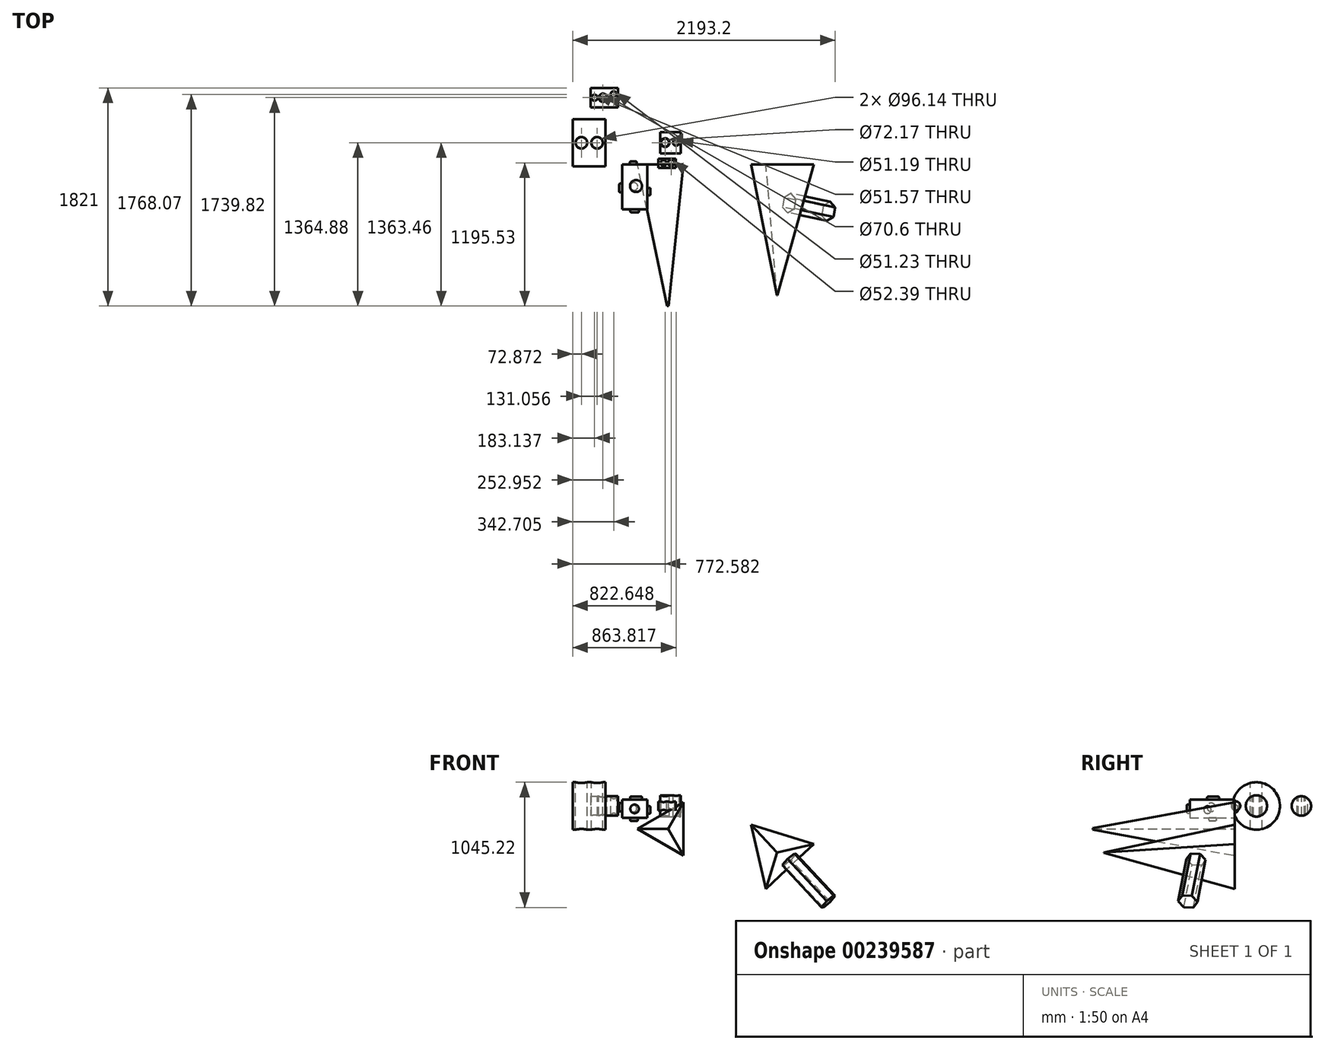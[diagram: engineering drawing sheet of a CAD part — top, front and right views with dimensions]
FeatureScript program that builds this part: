
annotation { "Feature Type Name" : "Feature", "Feature Type Description" : "" }
export const myFeature = defineFeature(function(context is Context, id is Id, definition is map)
    precondition{}
    {
        {
            var Q0;
            Q0=qCreatedBy(makeId("Front.planeOp"),FACE);
            var sketch = newSketch(context, id + "F0", { "sketchPlane" : qUnion([Q0])});
            skLineSegment(sketch, "E0", {"start": v(-145.02, 0) * mm, "end": v(178.73, 0) * mm});
            skLineSegment(sketch, "E1", {"start": v(-204, 52.6) * mm, "end": v(227.6, 52.6) * mm});
            skLineSegment(sketch, "E2", {"start": v(228.05, -98.9) * mm, "end": v(-210.3, -98.9) * mm});
            skLineSegment(sketch, "E3", {"start": v(81.85, 196.23) * mm, "end": v(81.85, -166.27) * mm});
            skLineSegment(sketch, "E4", {"start": v(-128.62, 137.85) * mm, "end": v(-128.62, -208.02) * mm});
            skSolve(sketch);
        }
        {
            var Q0;
            Q0 = qSketchRegion(id + "F0", true);
            extrude(context, id + "F1", {"entities" : qUnion([Q0]), "depth" : 373.9 * mm});
        }
        {
            var Q0;
            Q0=makeQuery(id+"F1.opExtrude","CAP_FACE",FACE,{"disambiguationData":[OSD([sQuery(id+"F0.wireOp",EDGE,"E1"),sQuery(id+"F0.wireOp",EDGE,"E2"),sQuery(id+"F0.wireOp",EDGE,"E3"),sQuery(id+"F0.wireOp",EDGE,"E4")])],"isStart":false});
            var sketch = newSketch(context, id + "F2", { "sketchPlane" : qUnion([Q0])});
            skCircle(sketch, "E5", {"center": v(-25.3, -24.2) * mm, "radius": 35.87 * mm});
            skSolve(sketch);
        }
        {
            var Q0;
            Q0 = qSketchRegion(id + "F2", true);
            extrude(context, id + "F3", {"entities" : qUnion([Q0]), "operationType" : NewBodyOperationType.ADD, "depth" : 25.4 * mm});
        }
        {
            var Q0;
            Q0=makeQuery(id+"F1.opExtrude","SWEPT_FACE",FACE,{"disambiguationData":[OSD([sQuery(id+"F0.wireOp",EDGE,"E3")])]});
            var sketch = newSketch(context, id + "F4", { "sketchPlane" : qUnion([Q0])});
            skCircle(sketch, "E6", {"center": v(-226.15, -32.57) * mm, "radius": 30.45 * mm});
            skSolve(sketch);
        }
        {
            var Q0;
            Q0 = qSketchRegion(id + "F4", true);
            extrude(context, id + "F5", {"entities" : qUnion([Q0]), "operationType" : NewBodyOperationType.ADD, "depth" : 25.4 * mm});
        }
        {
            var Q0;
            Q0=makeQuery(id+"F1.opExtrude","CAP_FACE",FACE,{"disambiguationData":[OSD([sQuery(id+"F0.wireOp",EDGE,"E1"),sQuery(id+"F0.wireOp",EDGE,"E2"),sQuery(id+"F0.wireOp",EDGE,"E3"),sQuery(id+"F0.wireOp",EDGE,"E4")])],"isStart":true});
            var sketch = newSketch(context, id + "F27", { "sketchPlane" : qUnion([Q0])});
            skCircle(sketch, "E7", {"center": v(36.05, -21.8) * mm, "radius": 28.54 * mm});
            skSolve(sketch);
        }
        {
            var Q0;
            Q0 = qSketchRegion(id + "F27", true);
            extrude(context, id + "F6", {"entities" : qUnion([Q0]), "operationType" : NewBodyOperationType.ADD, "depth" : 25.4 * mm});
        }
        {
            var Q0;
            Q0=makeQuery(id+"F1.opExtrude","SWEPT_FACE",FACE,{"disambiguationData":[OSD([sQuery(id+"F0.wireOp",EDGE,"E4")])]});
            var sketch = newSketch(context, id + "F7", { "sketchPlane" : qUnion([Q0])});
            skCircle(sketch, "E8", {"center": v(195.22, -10.7) * mm, "radius": 35.87 * mm});
            skSolve(sketch);
        }
        {
            var Q0;
            Q0 = qSketchRegion(id + "F7", true);
            extrude(context, id + "F8", {"entities" : qUnion([Q0]), "operationType" : NewBodyOperationType.ADD, "depth" : 25.4 * mm});
        }
        {
            var Q0;
            Q0=makeQuery(id+"F1.opExtrude","SWEPT_FACE",FACE,{"disambiguationData":[OSD([sQuery(id+"F0.wireOp",EDGE,"E1")])]});
            var sketch = newSketch(context, id + "F28", { "sketchPlane" : qUnion([Q0])});
            skCircle(sketch, "E9", {"center": v(-13.2, -179.26) * mm, "radius": 50 * mm});
            skSolve(sketch);
        }
        {
            var Q0;
            Q0 = qSketchRegion(id + "F28", true);
            extrude(context, id + "F9", {"entities" : qUnion([Q0]), "operationType" : NewBodyOperationType.ADD, "depth" : 25.4 * mm});
        }
        {
            var Q0;
            Q0=makeQuery(id+"F1.opExtrude","SWEPT_FACE",FACE,{"disambiguationData":[OSD([sQuery(id+"F0.wireOp",EDGE,"E2")])]});
            var sketch = newSketch(context, id + "F10", { "sketchPlane" : qUnion([Q0])});
            skCircle(sketch, "E10", {"center": v(-29.94, 183.6) * mm, "radius": 31.67 * mm});
            skSolve(sketch);
        }
        {
            var Q0;
            Q0 = qSketchRegion(id + "F10", true);
            extrude(context, id + "F11", {"entities" : qUnion([Q0]), "operationType" : NewBodyOperationType.ADD, "depth" : 25.4 * mm});
        }
        {
            var Q0;
            Q0=makeQuery(id+"F11.opExtrude","CAP_EDGE",EDGE,{"disambiguationData":[OSD([sQuery(id+"F10.wireOp",EDGE,"E10")])],"isStart":false});
            var Q1;
            Q1=makeQuery(id+"F8.opExtrude","CAP_EDGE",EDGE,{"disambiguationData":[OSD([sQuery(id+"F7.wireOp",EDGE,"E8")])],"isStart":false});
            var Q2;
            Q2=makeQuery(id+"F3.opExtrude","CAP_EDGE",EDGE,{"disambiguationData":[OSD([sQuery(id+"F2.wireOp",EDGE,"E5")])],"isStart":false});
            var Q3;
            Q3=makeQuery(id+"F6.opExtrude","CAP_EDGE",EDGE,{"disambiguationData":[OSD([sQuery(id+"F27.wireOp",EDGE,"E7")])],"isStart":false});
            var Q4;
            Q4=makeQuery(id+"F9.opExtrude","CAP_EDGE",EDGE,{"disambiguationData":[OSD([sQuery(id+"F28.wireOp",EDGE,"E9")])],"isStart":false});
            var Q5;
            Q5=makeQuery(id+"F5.opExtrude","CAP_EDGE",EDGE,{"disambiguationData":[OSD([sQuery(id+"F4.wireOp",EDGE,"E6")])],"isStart":false});
            fillet(context, id + "F12", {"entities" : qUnion([Q0, Q1, Q2, Q3, Q4, Q5]), "radius" : 7.95 * mm, "tangentPropagation" : true, "allowEdgeOverflow" : false});
        }
        {
            var Q0;
            Q0=qCreatedBy(makeId("Front.planeOp"),FACE);
            var sketch = newSketch(context, id + "F29", { "sketchPlane" : qUnion([Q0])});
            skCircle(sketch, "E11.cCircle", {"center": v(254.78, -191.8) * mm, "radius": 128.13 * mm, "construction": true});
            skLineSegment(sketch, "E11.0", {"start": v(382.92, 30.13) * mm, "end": v(382.92, -413.74) * mm});
            skLineSegment(sketch, "E11.1", {"start": v(382.92, -413.74) * mm, "end": v(-1.48, -191.8) * mm});
            skLineSegment(sketch, "E11.2", {"start": v(-1.48, -191.8) * mm, "end": v(382.92, 30.13) * mm});
            skPoint(sketch, "E11.0.midPoint", {"position": v(382.92, -191.8) * mm});
            skSolve(sketch);
        }
        {
            var Q0;
            Q0 = qSketchRegion(id + "F29", true);
            extrude(context, id + "F30", {"entities" : qUnion([Q0]), "depth" : 1182.1 * mm, "hasDraft" : true, "draftAngle" : 6 * degree, "draftPullDirection" : true});
        }
        {
            var Q0;
            Q0=qCreatedBy(makeId("Front.planeOp"),FACE);
            var sketch = newSketch(context, id + "F31", { "sketchPlane" : qUnion([Q0])});
            skCircle(sketch, "E12.cCircle", {"center": v(1163.63, -389.04) * mm, "radius": 316.45 * mm, "construction": true});
            skLineSegment(sketch, "E12.0", {"start": v(947.84, -157.57) * mm, "end": v(1471.98, -317.9) * mm});
            skLineSegment(sketch, "E12.1", {"start": v(1471.98, -317.9) * mm, "end": v(1071.05, -691.65) * mm});
            skLineSegment(sketch, "E12.2", {"start": v(1071.05, -691.65) * mm, "end": v(947.84, -157.57) * mm});
            skSolve(sketch);
        }
        {
            var Q0;
            Q0 = qSketchRegion(id + "F31", true);
            extrude(context, id + "F13", {"entities" : qUnion([Q0]), "depth" : 1090.3 * mm, "hasDraft" : true, "draftAngle" : 8.2 * degree, "draftPullDirection" : true});
        }
        {
            var Q0;
            Q0=makeQuery(id+"F13.opExtrude","SWEPT_FACE",FACE,{"disambiguationData":[OSD([sQuery(id+"F31.wireOp",EDGE,"E12.1")])]});
            var sketch = newSketch(context, id + "F32", { "sketchPlane" : qUnion([Q0])});
            skCircle(sketch, "E13.cCircle", {"center": v(596.84, 229.06) * mm, "radius": 81.13 * mm, "construction": true});
            skLineSegment(sketch, "E13.0", {"start": v(674.4, 205.25) * mm, "end": v(615, 150) * mm});
            skLineSegment(sketch, "E13.1", {"start": v(615, 150) * mm, "end": v(537.44, 173.8) * mm});
            skLineSegment(sketch, "E13.2", {"start": v(537.44, 173.8) * mm, "end": v(519.29, 252.87) * mm});
            skLineSegment(sketch, "E13.3", {"start": v(519.29, 252.87) * mm, "end": v(578.68, 308.13) * mm});
            skLineSegment(sketch, "E13.4", {"start": v(578.68, 308.13) * mm, "end": v(656.24, 284.32) * mm});
            skLineSegment(sketch, "E13.5", {"start": v(656.24, 284.32) * mm, "end": v(674.4, 205.25) * mm});
            skSolve(sketch);
        }
        {
            var Q0;
            Q0 = qSketchRegion(id + "F32", true);
            extrude(context, id + "F33", {"entities" : qUnion([Q0]), "operationType" : NewBodyOperationType.ADD, "depth" : 484.65 * mm});
        }
        {
            var Q0;
            Q0=makeQuery(id+"F30.opExtrude","SWEPT_FACE",FACE,{"disambiguationData":[OSD([sQuery(id+"F29.wireOp",EDGE,"E11.2")])]});
            var sketch = newSketch(context, id + "F34", { "sketchPlane" : qUnion([Q0])});
            skLineSegment(sketch, "E14", {"start": v(0, -1597.82) * mm, "end": v(378.9, -670.38) * mm});
            skLineSegment(sketch, "E15", {"start": v(378.9, -670.38) * mm, "end": v(0, 0) * mm});
            skLineSegment(sketch, "E16", {"start": v(0, -1597.82) * mm, "end": v(-500.03, -1222.61) * mm});
            skLineSegment(sketch, "E17", {"start": v(-500.03, -1222.61) * mm, "end": v(0, 0) * mm});
            skLineSegment(sketch, "E18", {"start": v(-1117.83, -1371.82) * mm, "end": v(-374.13, 421.13) * mm, "construction": true});
            skSolve(sketch);
        }
        {
            var Q0;
            Q0 = qSketchRegion(id + "F34", true);
            var Q1;
            Q1=sQuery(id+"F34.wireOp",EDGE,"E17");
            var Q2;
            Q2=sQuery(id+"F34.wireOp",EDGE,"E16");
            var Q3;
            Q3=sQuery(id+"F34.wireOp",EDGE,"E14");
            var Q4;
            Q4=sQuery(id+"F34.wireOp",EDGE,"E15");
            var Q5;
            Q5=sQuery(id+"F34.wireOp",EDGE,"E18");
            revolve(context, id + "F14", {"bodyType" : ToolBodyType.SURFACE, "entities" : qUnion([Q0]), "surfaceEntities" : qUnion([Q1, Q2, Q3, Q4]), "axis" : qUnion([Q5]), "revolveType" : RevolveType.SYMMETRIC, "angle" : 97.05 * degree});
        }
        {
            var Q0;
            Q0=qCreatedBy(makeId("Top.planeOp"),FACE);
            var sketch = newSketch(context, id + "F35", { "sketchPlane" : qUnion([Q0])});
            skLineSegment(sketch, "E19.bottom", {"start": v(171.87, -28.46) * mm, "end": v(318.72, -28.46) * mm});
            skLineSegment(sketch, "E19.top", {"start": v(171.87, 9.86) * mm, "end": v(318.72, 9.86) * mm});
            skLineSegment(sketch, "E19.left", {"start": v(171.87, -28.46) * mm, "end": v(171.87, 9.86) * mm});
            skLineSegment(sketch, "E19.right", {"start": v(318.72, -28.46) * mm, "end": v(318.72, 9.86) * mm});
            skSolve(sketch);
        }
        {
            var Q0;
            Q0 = qSketchRegion(id + "F35", true);
            var Q1;
            Q1=sQuery(id+"F35.wireOp",EDGE,"E19.top");
            revolve(context, id + "F15", {"entities" : qUnion([Q0]), "axis" : qUnion([Q1]), "revolveType" : RevolveType.FULL});
        }
        {
            var Q0;
            Q0=qCreatedBy(makeId("Top.planeOp"),FACE);
            var sketch = newSketch(context, id + "F36", { "sketchPlane" : qUnion([Q0])});
            skCircle(sketch, "E20", {"center": v(216.64, 12.77) * mm, "radius": 24.12 * mm});
            skLineSegment(sketch, "E21", {"start": v(171.87, 48.19) * mm, "end": v(318.72, 48.19) * mm});
            skLineSegment(sketch, "E22", {"start": v(318.72, -28.46) * mm, "end": v(171.87, -28.46) * mm});
            skCircle(sketch, "E23", {"center": v(280, 13.44) * mm, "radius": 26.2 * mm});
            skSolve(sketch);
        }
        {
            var Q0;
            Q0 = qSketchRegion(id + "F36", true);
            extrude(context, id + "F16", {"entities" : qUnion([Q0]), "operationType" : NewBodyOperationType.REMOVE, "endBound" : BoundingType.UP_TO_NEXT, "depth" : 39.7 * mm, "hasSecondDirection" : true, "secondDirectionBound" : SecondDirectionBoundingType.UP_TO_NEXT, "secondDirectionOppositeDirection" : true, "secondDirectionDepth" : 25.4 * mm});
        }
        {
            var Q0;
            Q0=qCreatedBy(makeId("Top.planeOp"),FACE);
            var sketch = newSketch(context, id + "F37", { "sketchPlane" : qUnion([Q0])});
            skLineSegment(sketch, "E24.bottom", {"start": v(188.21, 182.79) * mm, "end": v(361.26, 182.79) * mm});
            skLineSegment(sketch, "E24.top", {"start": v(188.21, 271.54) * mm, "end": v(361.26, 271.54) * mm});
            skLineSegment(sketch, "E24.left", {"start": v(188.21, 182.79) * mm, "end": v(188.21, 271.54) * mm});
            skLineSegment(sketch, "E24.right", {"start": v(361.26, 182.79) * mm, "end": v(361.26, 271.54) * mm});
            skLineSegment(sketch, "E25", {"start": v(443.07, 182.79) * mm, "end": v(124.45, 182.79) * mm, "construction": true});
            skSolve(sketch);
        }
        {
            var Q0;
            Q0 = qSketchRegion(id + "F37", true);
            var Q1;
            Q1=sQuery(id+"F37.wireOp",EDGE,"E25");
            revolve(context, id + "F38", {"entities" : qUnion([Q0]), "axis" : qUnion([Q1]), "revolveType" : RevolveType.FULL});
        }
        {
            var Q0;
            Q0=qCreatedBy(makeId("Top.planeOp"),FACE);
            var sketch = newSketch(context, id + "F17", { "sketchPlane" : qUnion([Q0])});
            skCircle(sketch, "E26", {"center": v(229.94, 182.79) * mm, "radius": 33.9 * mm});
            skCircle(sketch, "E27", {"center": v(229.94, 182.79) * mm, "radius": 36.09 * mm});
            skLineSegment(sketch, "E28.0", {"start": v(443.07, 182.79) * mm, "end": v(124.45, 182.79) * mm});
            skCircle(sketch, "E29", {"center": v(321.18, 182.79) * mm, "radius": 25.6 * mm});
            skSolve(sketch);
        }
        {
            var Q0;
            Q0 = qSketchRegion(id + "F17", true);
            extrude(context, id + "F18", {"entities" : qUnion([Q0]), "operationType" : NewBodyOperationType.REMOVE, "endBound" : BoundingType.UP_TO_NEXT, "oppositeDirection" : true, "depth" : 25.4 * mm, "hasSecondDirection" : true, "secondDirectionBound" : SecondDirectionBoundingType.UP_TO_NEXT, "secondDirectionOppositeDirection" : false, "secondDirectionDepth" : 25.4 * mm});
        }
        {
            var Q0;
            Q0=qCreatedBy(makeId("Top.planeOp"),FACE);
            var sketch = newSketch(context, id + "F19", { "sketchPlane" : qUnion([Q0])});
            skLineSegment(sketch, "E30", {"start": v(-619.17, 181.37) * mm, "end": v(-207.92, 181.37) * mm, "construction": true});
            skLineSegment(sketch, "E31.bottom", {"start": v(-542.64, 181.37) * mm, "end": v(-269, 181.37) * mm});
            skLineSegment(sketch, "E31.top", {"start": v(-542.64, 379.31) * mm, "end": v(-269, 379.31) * mm});
            skLineSegment(sketch, "E31.left", {"start": v(-542.64, 181.37) * mm, "end": v(-542.64, 379.31) * mm});
            skLineSegment(sketch, "E31.right", {"start": v(-269, 181.37) * mm, "end": v(-269, 379.31) * mm});
            skSolve(sketch);
        }
        {
            var Q0;
            Q0 = qSketchRegion(id + "F19", true);
            var Q1;
            Q1=sQuery(id+"F19.wireOp",EDGE,"E30");
            revolve(context, id + "F39", {"entities" : qUnion([Q0]), "axis" : qUnion([Q1]), "revolveType" : RevolveType.FULL});
        }
        {
            var Q0;
            Q0=qCreatedBy(makeId("Top.planeOp"),FACE);
            var sketch = newSketch(context, id + "F40", { "sketchPlane" : qUnion([Q0])});
            skLineSegment(sketch, "E32.0", {"start": v(-619.17, 181.37) * mm, "end": v(-207.92, 181.37) * mm});
            skCircle(sketch, "E33", {"center": v(-469.77, 181.37) * mm, "radius": 48.07 * mm});
            skCircle(sketch, "E34", {"center": v(-338.71, 181.37) * mm, "radius": 48.07 * mm});
            skSolve(sketch);
        }
        {
            var Q0;
            Q0 = qSketchRegion(id + "F40", true);
            extrude(context, id + "F20", {"entities" : qUnion([Q0]), "operationType" : NewBodyOperationType.REMOVE, "endBound" : BoundingType.UP_TO_NEXT, "oppositeDirection" : true, "depth" : 25.4 * mm, "hasSecondDirection" : true, "secondDirectionBound" : SecondDirectionBoundingType.UP_TO_NEXT, "secondDirectionOppositeDirection" : false, "secondDirectionDepth" : 25.4 * mm});
        }
        {
            var Q0;
            Q0=qCreatedBy(makeId("Top.planeOp"),FACE);
            var sketch = newSketch(context, id + "F21", { "sketchPlane" : qUnion([Q0])});
            skLineSegment(sketch, "E35", {"start": v(-455.08, 557.73) * mm, "end": v(-209.18, 557.73) * mm, "construction": true});
            skLineSegment(sketch, "E36.bottom", {"start": v(-391.88, 557.73) * mm, "end": v(-164.56, 557.73) * mm});
            skLineSegment(sketch, "E36.top", {"start": v(-391.88, 638.91) * mm, "end": v(-164.56, 638.91) * mm});
            skLineSegment(sketch, "E36.left", {"start": v(-391.88, 557.73) * mm, "end": v(-391.88, 638.91) * mm});
            skLineSegment(sketch, "E36.right", {"start": v(-164.56, 557.73) * mm, "end": v(-164.56, 638.91) * mm});
            skSolve(sketch);
        }
        {
            var Q0;
            Q0 = qSketchRegion(id + "F21", true);
            var Q1;
            Q1=sQuery(id+"F21.wireOp",EDGE,"E35");
            revolve(context, id + "F22", {"entities" : qUnion([Q0]), "axis" : qUnion([Q1]), "revolveType" : RevolveType.FULL});
        }
        {
            var Q0;
            Q0=qCreatedBy(makeId("Top.planeOp"),FACE);
            var sketch = newSketch(context, id + "F23", { "sketchPlane" : qUnion([Q0])});
            skLineSegment(sketch, "E37.0", {"start": v(-455.08, 557.73) * mm, "end": v(-209.18, 557.73) * mm});
            skCircle(sketch, "E38", {"center": v(-359.5, 557.73) * mm, "radius": 25.79 * mm});
            skCircle(sketch, "E39", {"center": v(-289.69, 557.73) * mm, "radius": 35.3 * mm});
            skCircle(sketch, "E40", {"center": v(-199.94, 585.98) * mm, "radius": 25.62 * mm});
            skSolve(sketch);
        }
        {
            var Q0;
            Q0 = qSketchRegion(id + "F23", true);
            extrude(context, id + "F24", {"entities" : qUnion([Q0]), "operationType" : NewBodyOperationType.REMOVE, "endBound" : BoundingType.UP_TO_NEXT, "oppositeDirection" : true, "depth" : 25.4 * mm, "hasSecondDirection" : true, "secondDirectionBound" : SecondDirectionBoundingType.UP_TO_NEXT, "secondDirectionOppositeDirection" : false, "secondDirectionDepth" : 25.4 * mm});
        }
    });
